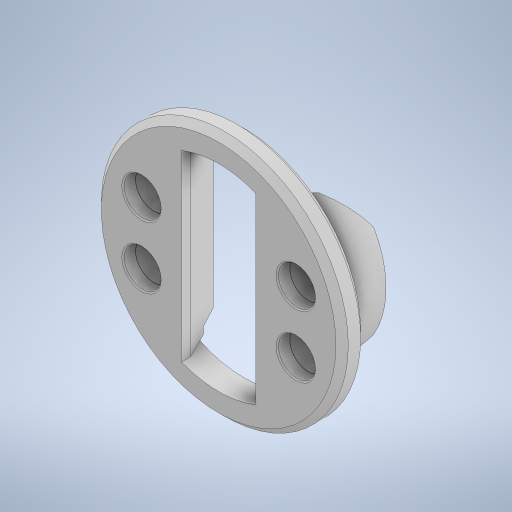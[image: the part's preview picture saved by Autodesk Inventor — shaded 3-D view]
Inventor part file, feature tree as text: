
AUTODESK INVENTOR PART (.ipt)
format: ipt  version: 2023.4 (Build 274418000, 418)  size: 354,304 bytes
history: native  units: mm
features: extrude x6, sketch x6, chamfer x5
ambient origin geometry x8: Origin, YZ Plane, XZ Plane, XY Plane, X Axis, Y Axis, Z Axis, Center Point
bodies: Solid1 (feature_tree)
feature tree (17):
  extrude  "Extrusion1"  Depth=7.1mm TaperAngle=0.0deg
  extrude  "Extrusion2"  Depth=1.0mm TaperAngle=0.0deg
  extrude  "Extrusion3"  Depth=4.0mm TaperAngle=0.0deg
  extrude  "Extrusion4"  Depth=2.0mm
  chamfer  "Chamfer1"  Distance=1.0mm
  chamfer  "Chamfer3"  Distance=2.0mm Angle=45.0deg
  extrude  "Extrusion5"  Depth=5.0mm
  extrude  "Extrusion6"  Depth=3.1mm
  chamfer  "Chamfer4"  [1 undecoded]
  chamfer  "Chamfer5"  Distance=6.0mm
  chamfer  "Chamfer8"  Distance=6.0mm
  sketch  "Sketch1"  dims[d0=30.05mm d1=7.1mm d2=0.0mm]
  sketch  "Sketch2"  dims[d3=32.0mm d4=1.0mm d5=0.0mm]
  sketch  "Sketch3"  dims[d6=40.0mm d7=4.0mm d8=0.0mm]
  sketch  "Sketch4"  dims[d9=6.0mm d10=6.0mm d11=1.0mm d12=0.0mm d13=7.0mm d14=2.0mm d15=45.0deg]
  sketch  "Sketch6"  dims[d19=1.0mm d20=2.0mm d21=45.0deg d22=5.0mm]
  sketch  "Sketch7"  dims[d23=12.5mm d24=3.1mm d25=0.0mm d26=0.0mm d27=6.0mm d28=6.0mm d29=6.0mm d30=6.0mm d31=2.0mm d32=0.0mm d33=1.4mm d34=2.0mm d35=45.0deg d36=0.2mm d37=2.0mm d38=45.0deg d45=3.6mm d46=2.0mm d47=45.0deg]
note: 1 required parameter value undecoded (feature->parameter linkage not recoverable at this tier; creation-order binding heuristic only, values carry confidence <= 0.55)
